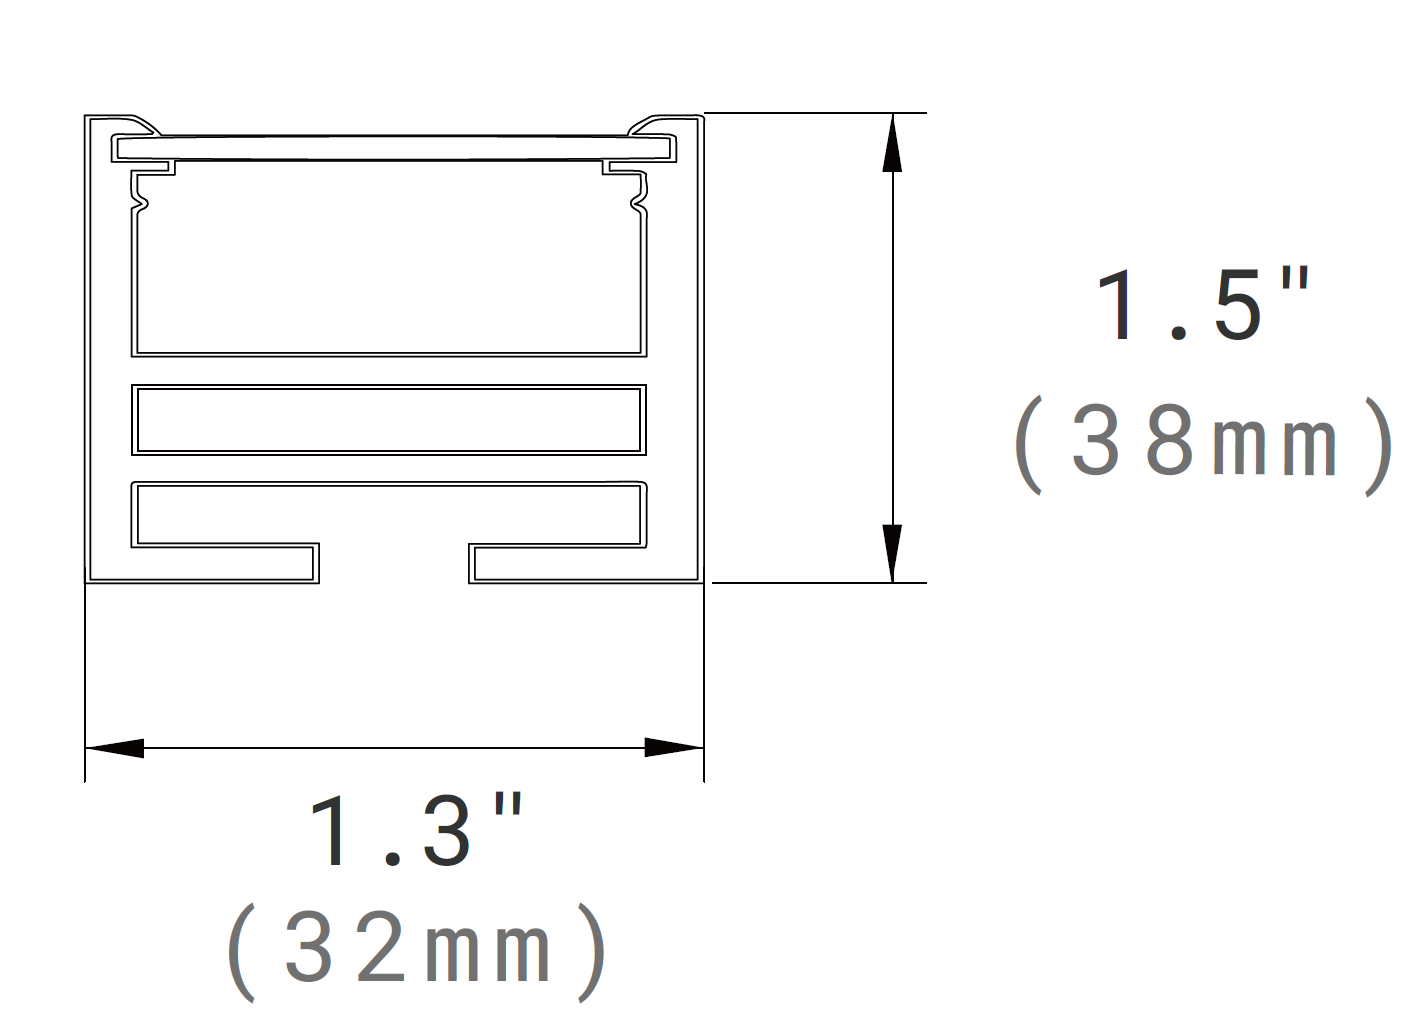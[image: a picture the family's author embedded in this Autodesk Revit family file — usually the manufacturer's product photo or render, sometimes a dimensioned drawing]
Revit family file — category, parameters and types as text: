
# Revit family: VRD-DPMK
name_source: partatom
category: Lighting Fixtures
units: mm (PartAtom-declared; Revit-internal decimal feet)

## family parameters
Cut with Voids When Loaded = Yes
Host = Face
Light Source = Yes
Maintain Annotation Orientation = No
Part Type = Normal
Room Calculation Point = No
Round Connector Dimension = Use Diameter
Shared = No

## types (9) — shared parameters
1/2D1 = 0' - 5"
10'' Canopy 1 = Yes
Beam Angle = 0.00°
CRI = 90
Color Filter = 16777215
D1 = 0' - 10"
Default Elevation = 0' - 0"
Dimming Lamp Color Temperature Shift = <None>
Input Voltage = 120-277V
Lamp = LED
Load Classification = Lighting
Manufacturer = Above All Lighting
Power Factor = 0.9
Suspension = 3' - 0"
Tilt Angle = 90.00°
URL = https://www.abovealllighting.com

## per-type parameters (varying)
| type | 10'' Canopy 2 | 10'' Canopy 3 | Cable Count | Canopy R | Model | Photometric Web File | R | Wattage Comments | cable |
| VRD-40W-4000K-ACPMK | No | No | 2 | 0' - 11 3/16" | VRD-4024-40901-ACPMK-WH | VRD-4024-40901 (1).IES | 0' - 11 13/16" | 40W | 0' - 11 25/32" |
| VRD-50W-3000K-ACPMK | No | No | 2 | 1' - 5 3/32" | VRD-5035-30901-ACPMK-WH | VRD_5035_30901.ies | 1' - 5 11/16" | 50W | 1' - 5 21/32" |
| VRD-80W-4000K-ACPMK | No | No | 3 | 1' - 11" | VRD-8047-40901-ACPMK-WH | VRD-8047-40901 (1).IES | 1' - 11 19/32" | 80W | 1' - 11 9/16" |
| VRD-100W-3000K-ACPMK | No | No | 3 | 2' - 4 15/16" | VRD-10059-30901-ACPMK-WH | VRD_10059_30901.ies | 2' - 5 9/16" | 100W | 2' - 5 17/32" |
| VRD-120W-3000K-ACPMK | No | Yes | 4 | 3' - 2 13/16" | VRD-12079-30901-ACPMK-WH | generic | 3' - 3 13/32" | 120W | 3' - 3 3/8" |
| VRD-160W-3000K-ACPMK | No | Yes | 6 | 4' - 0 19/32" | VRD-16098-30901-ACPMK-WH | generic | 4' - 1 3/16" | 160W | 4' - 1 5/32" |
| VRD-200W-3000K-ACPMK | Yes | Yes | 7 | 4' - 10 7/16" | VRD-200118-30901-ACPMK-WH | generic | 4' - 11 1/16" | 200W | 4' - 11 1/32" |
| VRD-300W-3000K-ACPMK | Yes | Yes | 9 | 6' - 6 13/32" | VRD-300158-30901-ACPMK-WH | generic | 6' - 7" | 300W | 6' - 6 31/32" |
| VRD-400W-3000K-ACPMK | Yes | Yes | 15 | 7' - 8 1/4" | VRD-400197-30901-ACPMK-WH | generic | 7' - 8 27/32" | 400W | 7' - 8 13/16" |

## geometry (parser evidence)
native form markers: Sweep x2
no freeform markers — native parametric forms only
